FCSTD DOCUMENT  (FreeCAD 1.0R39109 (Git))
Label: arm1
License: All rights reserved
LicenseURL: https://en.wikipedia.org/wiki/All_rights_reserved
objects: Sketcher::SketchObject×1, PartDesign::Body×1
note: 3 computed .brp shape members not serialized (recipe doc carries the construction recipe); baked Part::Feature solids carry a one-line shape summary decoded from their .brp

FEATURE [Sketcher::SketchObject] Sketch
  ArcFitTolerance = 1e-06
  AttachmentSupport = -> [XY_Plane]
  FullyConstrained = false
  MakeInternals = false
  MapMode = 5
  sketch-geometry (116):
    g0: LineSegment [constr] StartX=20.0632 StartY=3.7e-05 StartZ=0 EndX=20.0632 EndY=-40 EndZ=0
    g1: Circle [constr] CenterX=20.0632 CenterY=-20 CenterZ=0 NormalX=0 NormalY=0 NormalZ=1 AngleXU=0 Radius=14
    g2: LineSegment [constr] StartX=20.0632 StartY=-20 StartZ=0 EndX=20.0632 EndY=380 EndZ=0
    g3: ArcOfCircle CenterX=20.0632 CenterY=380 CenterZ=0 NormalX=0 NormalY=0 NormalZ=1 AngleXU=0 Radius=25 StartAngle=6.28319 EndAngle=9.42478
    g4: LineSegment [constr] StartX=20.0632 StartY=3.7e-05 StartZ=0 EndX=20.0632 EndY=5.00004 EndZ=0
    g5: Circle CenterX=20.0632 CenterY=380 CenterZ=0 NormalX=0 NormalY=0 NormalZ=1 AngleXU=0 Radius=5
    g6: LineSegment [constr] StartX=20.0632 StartY=-20 StartZ=0 EndX=-4.93685 EndY=-20 EndZ=0
    g7: LineSegment [constr] StartX=20.0632 StartY=-20 StartZ=0 EndX=45.0632 EndY=-20 EndZ=0
    g8: LineSegment StartX=-4.93685 StartY=-20 StartZ=0 EndX=-4.93685 EndY=380 EndZ=0
    g9: LineSegment StartX=45.0632 StartY=-20 StartZ=0 EndX=45.0632 EndY=380 EndZ=0
    g10: ArcOfCircle CenterX=20.0632 CenterY=-20.0003 CenterZ=0 NormalX=0 NormalY=0 NormalZ=1 AngleXU=0 Radius=25 StartAngle=3.14158 EndAngle=6.2832
    g11: LineSegment [constr] StartX=340.101 StartY=0 StartZ=0 EndX=340.101 EndY=-40 EndZ=0
    g12: Circle [constr] CenterX=340.101 CenterY=-20 CenterZ=0 NormalX=0 NormalY=0 NormalZ=1 AngleXU=0 Radius=14
    g13: LineSegment [constr] StartX=340.101 StartY=-20 StartZ=0 EndX=340.101 EndY=380 EndZ=0
    g14: ArcOfCircle CenterX=340.101 CenterY=380 CenterZ=0 NormalX=0 NormalY=0 NormalZ=1 AngleXU=0 Radius=25 StartAngle=0 EndAngle=1e-06
    g15: Circle CenterX=340.101 CenterY=380 CenterZ=0 NormalX=0 NormalY=0 NormalZ=1 AngleXU=0 Radius=5
    g16: LineSegment [constr] StartX=340.101 StartY=-20 StartZ=0 EndX=365.101 EndY=-20 EndZ=0
    g17: LineSegment [constr] StartX=340.101 StartY=-20 StartZ=0 EndX=315.101 EndY=-20 EndZ=0
    g18: LineSegment StartX=315.101 StartY=-20 StartZ=0 EndX=315.101 EndY=380 EndZ=0
    g19: LineSegment StartX=365.101 StartY=-20 StartZ=0 EndX=365.101 EndY=380 EndZ=0
    g20: ArcOfCircle CenterX=340.101 CenterY=380 CenterZ=0 NormalX=0 NormalY=0 NormalZ=1 AngleXU=0 Radius=25.0005 StartAngle=6.27666 EndAngle=9.42479
    g21: ArcOfCircle CenterX=340.101 CenterY=-20 CenterZ=0 NormalX=0 NormalY=0 NormalZ=1 AngleXU=0 Radius=25 StartAngle=3.14159 EndAngle=6.28319
    g22: Circle CenterX=340.101 CenterY=-20 CenterZ=0 NormalX=0 NormalY=0 NormalZ=1 AngleXU=0 Radius=5
    g23: Circle CenterX=20.0632 CenterY=380 CenterZ=0 NormalX=0 NormalY=0 NormalZ=1 AngleXU=0 Radius=2
    g24: Circle CenterX=340.101 CenterY=380 CenterZ=0 NormalX=0 NormalY=0 NormalZ=1 AngleXU=0 Radius=2
    g25: Circle CenterX=340.101 CenterY=-20 CenterZ=0 NormalX=0 NormalY=0 NormalZ=1 AngleXU=0 Radius=2
    g26: LineSegment [constr] StartX=440.101 StartY=0 StartZ=0 EndX=440.101 EndY=-40 EndZ=0
    g27: Circle [constr] CenterX=440.101 CenterY=-20 CenterZ=0 NormalX=0 NormalY=0 NormalZ=1 AngleXU=0 Radius=14
    g28: LineSegment [constr] StartX=440.101 StartY=-20 StartZ=0 EndX=440.101 EndY=380 EndZ=0
    g29: ArcOfCircle CenterX=440.101 CenterY=380 CenterZ=0 NormalX=0 NormalY=0 NormalZ=1 AngleXU=0 Radius=25 StartAngle=0 EndAngle=1e-06
    g30: Circle CenterX=440.101 CenterY=380 CenterZ=0 NormalX=0 NormalY=0 NormalZ=1 AngleXU=0 Radius=5
    g31: LineSegment [constr] StartX=440.101 StartY=-20 StartZ=0 EndX=465.101 EndY=-20 EndZ=0
    g32: LineSegment [constr] StartX=440.101 StartY=-20 StartZ=0 EndX=415.101 EndY=-20 EndZ=0
    g33: LineSegment StartX=415.101 StartY=-20 StartZ=0 EndX=415.101 EndY=380 EndZ=0
    g34: LineSegment StartX=465.101 StartY=-20 StartZ=0 EndX=465.101 EndY=380 EndZ=0
    g35: ArcOfCircle CenterX=440.101 CenterY=380 CenterZ=0 NormalX=0 NormalY=0 NormalZ=1 AngleXU=0 Radius=25.0005 StartAngle=6.27666 EndAngle=9.42479
    g36: ArcOfCircle CenterX=440.101 CenterY=-20 CenterZ=0 NormalX=0 NormalY=0 NormalZ=1 AngleXU=0 Radius=25 StartAngle=3.14159 EndAngle=6.28319
    g37: Circle CenterX=440.101 CenterY=-20 CenterZ=0 NormalX=0 NormalY=0 NormalZ=1 AngleXU=0 Radius=5
    g38: Circle CenterX=440.101 CenterY=380 CenterZ=0 NormalX=0 NormalY=0 NormalZ=1 AngleXU=0 Radius=2
    g39: Circle CenterX=440.101 CenterY=-20 CenterZ=0 NormalX=0 NormalY=0 NormalZ=1 AngleXU=0 Radius=2
    g40: LineSegment [constr] StartX=120.063 StartY=-20 StartZ=0 EndX=120.063 EndY=380 EndZ=0
    g41: ArcOfCircle CenterX=120.063 CenterY=380 CenterZ=0 NormalX=0 NormalY=0 NormalZ=1 AngleXU=0 Radius=25 StartAngle=1.228e-05 EndAngle=1.328e-05
    g42: Circle CenterX=120.063 CenterY=380 CenterZ=0 NormalX=0 NormalY=0 NormalZ=1 AngleXU=0 Radius=5
    g43: LineSegment StartX=95.0626 StartY=-20 StartZ=0 EndX=95.0626 EndY=380 EndZ=0
    g44: LineSegment StartX=145.063 StartY=-20 StartZ=0 EndX=145.063 EndY=380 EndZ=0
    g45: ArcOfCircle CenterX=120.063 CenterY=380 CenterZ=0 NormalX=0 NormalY=0 NormalZ=1 AngleXU=0 Radius=25.0005 StartAngle=6.27667 EndAngle=9.42478
    g46: Circle CenterX=120.063 CenterY=380 CenterZ=0 NormalX=0 NormalY=0 NormalZ=1 AngleXU=0 Radius=2
    g47: LineSegment [constr] StartX=120.063 StartY=3.7e-05 StartZ=0 EndX=120.063 EndY=-40 EndZ=0
    g48: Circle [constr] CenterX=120.063 CenterY=-20 CenterZ=0 NormalX=0 NormalY=0 NormalZ=1 AngleXU=0 Radius=14
    g49: LineSegment [constr] StartX=120.063 StartY=-20 StartZ=0 EndX=95.0632 EndY=-20 EndZ=0
    g50: ArcOfCircle CenterX=120.063 CenterY=-20 CenterZ=0 NormalX=0 NormalY=0 NormalZ=1 AngleXU=0 Radius=25 StartAngle=3.14159 EndAngle=6.28319
    g51: Circle [constr] CenterX=20.0632 CenterY=-20.0003 CenterZ=0 NormalX=0 NormalY=0 NormalZ=1 AngleXU=0 Radius=11
    g52: LineSegment [constr] StartX=20.0632 StartY=-20 StartZ=0 EndX=20.0632 EndY=-9.00027 EndZ=0
    g53: Circle CenterX=20.0632 CenterY=-9.00027 CenterZ=0 NormalX=0 NormalY=0 NormalZ=1 AngleXU=0 Radius=1.25
    g54: Circle CenterX=9.06345 CenterY=-20 CenterZ=0 NormalX=0 NormalY=0 NormalZ=1 AngleXU=0 Radius=1.25
    g55: Circle CenterX=20.0632 CenterY=-30.9997 CenterZ=0 NormalX=0 NormalY=0 NormalZ=1 AngleXU=0 Radius=1.25
    g56: Circle CenterX=31.0629 CenterY=-20 CenterZ=0 NormalX=0 NormalY=0 NormalZ=1 AngleXU=0 Radius=1.25
    g57: LineSegment [constr] StartX=120.063 StartY=-20 StartZ=0 EndX=145.063 EndY=-20 EndZ=0
    g58: Circle [constr] CenterX=120.063 CenterY=-20.0003 CenterZ=0 NormalX=0 NormalY=0 NormalZ=1 AngleXU=0 Radius=11
    g59: Circle CenterX=131.063 CenterY=-20 CenterZ=0 NormalX=0 NormalY=0 NormalZ=1 AngleXU=0 Radius=1.25
    g60: Circle CenterX=120.063 CenterY=-9.00027 CenterZ=0 NormalX=0 NormalY=0 NormalZ=1 AngleXU=0 Radius=1.25
    g61: Circle CenterX=109.063 CenterY=-20 CenterZ=0 NormalX=0 NormalY=0 NormalZ=1 AngleXU=0 Radius=1.25
    g62: Circle CenterX=120.063 CenterY=-30.9997 CenterZ=0 NormalX=0 NormalY=0 NormalZ=1 AngleXU=0 Radius=1.25
    g63: Circle CenterX=351.101 CenterY=-20 CenterZ=0 NormalX=0 NormalY=0 NormalZ=1 AngleXU=0 Radius=1.25
    g64: Circle [constr] CenterX=340.101 CenterY=-20.0003 CenterZ=0 NormalX=0 NormalY=0 NormalZ=1 AngleXU=0 Radius=11
    g65: Circle CenterX=340.101 CenterY=-9.0003 CenterZ=0 NormalX=0 NormalY=0 NormalZ=1 AngleXU=0 Radius=1.25
    g66: Circle CenterX=329.101 CenterY=-20 CenterZ=0 NormalX=0 NormalY=0 NormalZ=1 AngleXU=0 Radius=1.25
    g67: Circle CenterX=340.101 CenterY=-30.9997 CenterZ=0 NormalX=0 NormalY=0 NormalZ=1 AngleXU=0 Radius=1.25
    g68: Circle [constr] CenterX=440.101 CenterY=-20 CenterZ=0 NormalX=0 NormalY=0 NormalZ=1 AngleXU=0 Radius=11
    g69: Circle CenterX=451.101 CenterY=-19.9997 CenterZ=0 NormalX=0 NormalY=0 NormalZ=1 AngleXU=0 Radius=1.25
    g70: Circle CenterX=440.101 CenterY=-9 CenterZ=0 NormalX=0 NormalY=0 NormalZ=1 AngleXU=0 Radius=1.25
    g71: Circle CenterX=429.101 CenterY=-19.9997 CenterZ=0 NormalX=0 NormalY=0 NormalZ=1 AngleXU=0 Radius=1.25
    g72: Circle CenterX=440.101 CenterY=-30.9994 CenterZ=0 NormalX=0 NormalY=0 NormalZ=1 AngleXU=0 Radius=1.25
    g73: LineSegment [constr] StartX=40.2 StartY=0.900035 StartZ=0 EndX=40.2 EndY=62 EndZ=0
    g74: LineSegment [constr] StartX=20.1 StartY=6.5 StartZ=0 EndX=34.6 EndY=6.5 EndZ=0
    g75: LineSegment StartX=34.6 StartY=6.5 StartZ=0 EndX=5.6 EndY=6.5 EndZ=0
    g76: LineSegment StartX=34.6 StartY=6.5 StartZ=0 EndX=34.6 EndY=62 EndZ=0
    g77: Circle CenterX=31.1 CenterY=3.7 CenterZ=0 NormalX=0 NormalY=0 NormalZ=1 AngleXU=0 Radius=1.25
    g78: Circle CenterX=37.4 CenterY=53 CenterZ=0 NormalX=0 NormalY=0 NormalZ=1 AngleXU=0 Radius=1.25
    g79: Circle CenterX=37.4 CenterY=31 CenterZ=0 NormalX=0 NormalY=0 NormalZ=1 AngleXU=0 Radius=1.25
    g80: Circle CenterX=37.4 CenterY=9 CenterZ=0 NormalX=0 NormalY=0 NormalZ=1 AngleXU=0 Radius=1.25
    g81: Circle [constr] CenterX=20.1 CenterY=49 CenterZ=0 NormalX=0 NormalY=0 NormalZ=1 AngleXU=0 Radius=14
    g82: LineSegment [constr] StartX=0 StartY=0.900035 StartZ=0 EndX=40.2 EndY=0.900035 EndZ=0
    g83: ArcOfCircle CenterX=20.1 CenterY=49 CenterZ=0 NormalX=0 NormalY=0 NormalZ=1 AngleXU=0 Radius=14 StartAngle=1.19055 EndAngle=1.95105
    g84: LineSegment StartX=25.2962 StartY=62 StartZ=0 EndX=34.6 EndY=62 EndZ=0
    g85: LineSegment [constr] StartX=34.6 StartY=62 StartZ=0 EndX=40.2 EndY=62 EndZ=0
    g86: LineSegment [constr] StartX=0 StartY=62 StartZ=0 EndX=0 EndY=0.900035 EndZ=0
    g87: LineSegment StartX=5.6 StartY=6.5 StartZ=0 EndX=5.6 EndY=62 EndZ=0
    g88: Circle CenterX=2.8 CenterY=53 CenterZ=0 NormalX=0 NormalY=0 NormalZ=1 AngleXU=0 Radius=1.25
    g89: Circle CenterX=2.8 CenterY=31 CenterZ=0 NormalX=0 NormalY=0 NormalZ=1 AngleXU=0 Radius=1.25
    g90: Circle CenterX=2.8 CenterY=9 CenterZ=0 NormalX=0 NormalY=0 NormalZ=1 AngleXU=0 Radius=1.25
    g91: Circle CenterX=9.1 CenterY=3.7 CenterZ=0 NormalX=0 NormalY=0 NormalZ=1 AngleXU=0 Radius=1.25
    g92: LineSegment StartX=5.6 StartY=62 StartZ=0 EndX=14.9038 EndY=62 EndZ=0
    g93: LineSegment [constr] StartX=0 StartY=62 StartZ=0 EndX=5.6 EndY=62 EndZ=0
    g94: LineSegment [constr] StartX=99.9621 StartY=66.1 StartZ=0 EndX=140.162 EndY=66.1 EndZ=0
    g95: LineSegment [constr] StartX=140.162 StartY=66.1 StartZ=0 EndX=140.162 EndY=5.00003 EndZ=0
    g96: LineSegment [constr] StartX=120.062 StartY=60.5 StartZ=0 EndX=134.562 EndY=60.5 EndZ=0
    g97: LineSegment StartX=134.562 StartY=60.5 StartZ=0 EndX=105.562 EndY=60.5 EndZ=0
    g98: LineSegment StartX=134.562 StartY=60.5 StartZ=0 EndX=134.562 EndY=5.00003 EndZ=0
    g99: Circle CenterX=131.062 CenterY=63.3 CenterZ=0 NormalX=0 NormalY=0 NormalZ=1 AngleXU=0 Radius=1.25
    g100: Circle CenterX=137.362 CenterY=36 CenterZ=0 NormalX=0 NormalY=0 NormalZ=1 AngleXU=0 Radius=1.25
    g101: Circle CenterX=137.362 CenterY=58 CenterZ=0 NormalX=0 NormalY=0 NormalZ=1 AngleXU=0 Radius=1.25
    g102: LineSegment [constr] StartX=102.762 StartY=36 StartZ=0 EndX=137.362 EndY=36 EndZ=0
    g103: Circle [constr] CenterX=120.062 CenterY=18 CenterZ=0 NormalX=0 NormalY=0 NormalZ=1 AngleXU=0 Radius=14
    g104: Circle CenterX=137.362 CenterY=14 CenterZ=0 NormalX=0 NormalY=0 NormalZ=1 AngleXU=0 Radius=1.25
    g105: ArcOfCircle CenterX=120.062 CenterY=18 CenterZ=0 NormalX=0 NormalY=0 NormalZ=1 AngleXU=0 Radius=14 StartAngle=4.33214 EndAngle=5.09264
    g106: LineSegment [constr] StartX=140.162 StartY=5.00003 StartZ=0 EndX=134.562 EndY=5.00003 EndZ=0
    g107: LineSegment StartX=125.258 StartY=5.00003 StartZ=0 EndX=134.562 EndY=5.00003 EndZ=0
    g108: LineSegment StartX=105.562 StartY=60.5 StartZ=0 EndX=105.562 EndY=5.00004 EndZ=0
    g109: LineSegment [constr] StartX=99.9621 StartY=5.00004 StartZ=0 EndX=99.9621 EndY=66.1 EndZ=0
    g110: Circle CenterX=102.762 CenterY=36 CenterZ=0 NormalX=0 NormalY=0 NormalZ=1 AngleXU=0 Radius=1.25
    g111: Circle CenterX=102.762 CenterY=58 CenterZ=0 NormalX=0 NormalY=0 NormalZ=1 AngleXU=0 Radius=1.25
    g112: Circle CenterX=109.062 CenterY=63.3 CenterZ=0 NormalX=0 NormalY=0 NormalZ=1 AngleXU=0 Radius=1.25
    g113: Circle CenterX=102.762 CenterY=14 CenterZ=0 NormalX=0 NormalY=0 NormalZ=1 AngleXU=0 Radius=1.25
    g114: LineSegment [constr] StartX=99.9621 StartY=5.00004 StartZ=0 EndX=105.562 EndY=5.00004 EndZ=0
    g115: LineSegment StartX=105.562 StartY=5.00004 StartZ=0 EndX=114.866 EndY=5.00004 EndZ=0
  constraints (204):
    c: Distance(g0) = 40
    c: Vertical(g0)
    c: Diameter(g1) = 28
    c: Symmetric(g0,g0,g1)
    c: Distance(g2) = 400
    c: Coincident(g2,g1)
    c: Vertical(g2)
    c: Diameter(g3) = 50
    c: Coincident(g3,g2)
    c: Coincident(g4,g0)
    c: Vertical(g4)
    c: Diameter(g5) = 10
    c: Coincident(g5,g2)
    c: Coincident(g6,g1)
    c: PointOnObject(g6,g10)
    c: Horizontal(g6)
    c: Coincident(g7,g1)
    c: Horizontal(g7)
    c: Coincident(g8,g6)
    c: Vertical(g8)
    c: Coincident(g10,g7)
    c: PointOnObject(g10,g6)
    c: Coincident(g3,g9)
    c: Coincident(g3,g8)
    c: Vertical(g11)
    c: Diameter(g12) = 28
    c: Symmetric(g11,g11,g12)
    c: Coincident(g13,g12)
    c: Vertical(g13)
    c: Diameter(g14) = 50
    c: Coincident(g14,g13)
    c: Coincident(g15,g13)
    c: Coincident(g16,g12)
    c: Horizontal(g16)
    c: Coincident(g17,g12)
    c: PointOnObject(g17,g21)
    c: Horizontal(g17)
    c: Coincident(g19,g16)
    c: Vertical(g19)
    c: Coincident(g14,g19)
    c: Coincident(g20,g13)
    c: PointOnObject(g20,g19)
    c: Coincident(g20,g18)
    c: Coincident(g21,g16)
    c: PointOnObject(g21,g17)
    c: Diameter(g22) = 10
    c: Coincident(g22,g21)
    c: Diameter(g23) = 4
    c: Coincident(g23,g2)
    c: Diameter(g24) = 4
    c: Coincident(g24,g13)
    c: Diameter(g25) = 4
    c: Coincident(g25,g12)
    c: Vertical(g26)
    c: Diameter(g27) = 28
    c: Symmetric(g26,g26,g27)
    c: Coincident(g28,g27)
    c: Vertical(g28)
    c: Diameter(g29) = 50
    c: Coincident(g29,g28)
    c: Coincident(g30,g28)
    c: Coincident(g31,g27)
    c: Horizontal(g31)
    c: Coincident(g32,g27)
    c: PointOnObject(g32,g36)
    c: Horizontal(g32)
    c: Coincident(g34,g31)
    c: Vertical(g34)
    c: Coincident(g29,g34)
    c: Coincident(g35,g28)
    c: PointOnObject(g35,g34)
    c: Coincident(g35,g33)
    c: Coincident(g36,g31)
    c: PointOnObject(g36,g32)
    c: Diameter(g37) = 10
    c: Coincident(g37,g36)
    c: Diameter(g38) = 4
    c: Coincident(g38,g28)
    c: Diameter(g39) = 4
    c: Coincident(g39,g27)
    c: Vertical(g47)
    c: Diameter(g48) = 28
    c: Symmetric(g47,g47,g48)
    c: Coincident(g40,g48)
    c: Vertical(g40)
    c: Diameter(g41) = 50
    c: Coincident(g41,g40)
    c: Coincident(g42,g40)
    c: Coincident(g49,g48)
    c: PointOnObject(g49,g50)
    c: Horizontal(g49)
    c: Vertical(g44)
    c: Coincident(g41,g44)
    c: Coincident(g45,g40)
    c: PointOnObject(g45,g44)
    c: Coincident(g45,g43)
    c: PointOnObject(g50,g49)
    c: Diameter(g46) = 4
    c: Coincident(g46,g40)
    c: Diameter(g51) = 22
    c: Coincident(g51,g10)
    c: Coincident(g52,g1)
    c: PointOnObject(g52,g51)
    c: Vertical(g52)
    c: Diameter(g53) = 2.5
    c: Coincident(g53,g52)
    c: Diameter(g54) = 2.5
    c: Diameter(g55) = 2.5
    c: Diameter(g56) = 2.5
    c: Horizontal(g57)
    c: Diameter(g58) = 22
    c: Diameter(g60) = 2.5
    c: Diameter(g61) = 2.5
    c: Diameter(g62) = 2.5
    c: Diameter(g59) = 2.5
    c: Diameter(g64) = 22
    c: Diameter(g65) = 2.5
    c: Diameter(g66) = 2.5
    c: Diameter(g67) = 2.5
    c: Diameter(g63) = 2.5
    c: Diameter(g68) = 22
    c: Diameter(g70) = 2.5
    c: Diameter(g71) = 2.5
    c: Diameter(g72) = 2.5
    c: Diameter(g69) = 2.5
    c: Coincident(g82,g73)
    c: Coincident(g86,g82)
    c: Horizontal(g82)
    c: Vertical(g73)
    c: Vertical(g86)
    c: Distance(g73,g86) = 40.2
    c: Distance(g82,g86) = 61.1
    c: Diameter(g83) = 28
    c: Horizontal(g74)
    c: Coincident(g75,g74)
    c: Horizontal(g75)
    c: Coincident(g87,g75)
    c: Vertical(g87)
    c: Coincident(g76,g74)
    c: Vertical(g76)
    c: Diameter(g77) = 2.5
    c: Equal(g77,g91)
    c: Equal(g77,g78)
    c: Equal(g77,g88)
    c: Equal(g77,g89)
    c: Equal(g77,g90)
    c: Equal(g77,g80)
    c: Equal(g77,g79)
    c: Coincident(g81,g83)
    c: PointOnObject(g83,g81)
    c: Coincident(g84,g83)
    c: Coincident(g84,g76)
    c: Horizontal(g84)
    c: Coincident(g85,g76)
    c: Coincident(g85,g73)
    c: Horizontal(g85)
    c: Coincident(g92,g87)
    c: Coincident(g92,g83)
    c: Horizontal(g92)
    c: Coincident(g93,g86)
    c: Coincident(g93,g87)
    c: Horizontal(g93)
    c: DistanceY(g81,g2) = 331
    c: Coincident(g94,g95)
    c: Coincident(g109,g94)
    c: Horizontal(g94)
    c: Vertical(g95)
    c: Vertical(g109)
    c: Distance(g95,g109) = 40.2
    c: Distance(g94,g109) = 61.1
    c: Diameter(g105) = 28
    c: Horizontal(g96)
    c: Coincident(g97,g96)
    c: Horizontal(g97)
    c: Coincident(g108,g97)
    c: Vertical(g108)
    c: Coincident(g98,g96)
    c: Vertical(g98)
    c: Diameter(g99) = 2.5
    c: Equal(g99,g112)
    c: Equal(g99,g104)
    c: Equal(g99,g113)
    c: Equal(g99,g110)
    c: Equal(g99,g111)
    c: Equal(g99,g101)
    c: Equal(g99,g100)
    c: Coincident(g103,g105)
    c: PointOnObject(g105,g103)
    c: Coincident(g102,g110)
    c: Coincident(g102,g100)
    c: Horizontal(g102)
    c: Coincident(g114,g109)
    c: Coincident(g114,g108)
    c: Horizontal(g114)
    c: Coincident(g106,g95)
    c: Coincident(g106,g98)
    c: Horizontal(g106)
    c: Coincident(g107,g105)
    c: Coincident(g107,g98)
    c: Horizontal(g107)
    c: Coincident(g115,g108)
    c: Coincident(g115,g105)
    c: Horizontal(g115)
    c: DistanceY(g103,g40) = 362
FEATURE [PartDesign::Body] Body
  AllowCompound = false
  Group = -> [Sketch]
  Origin = -> Origin
